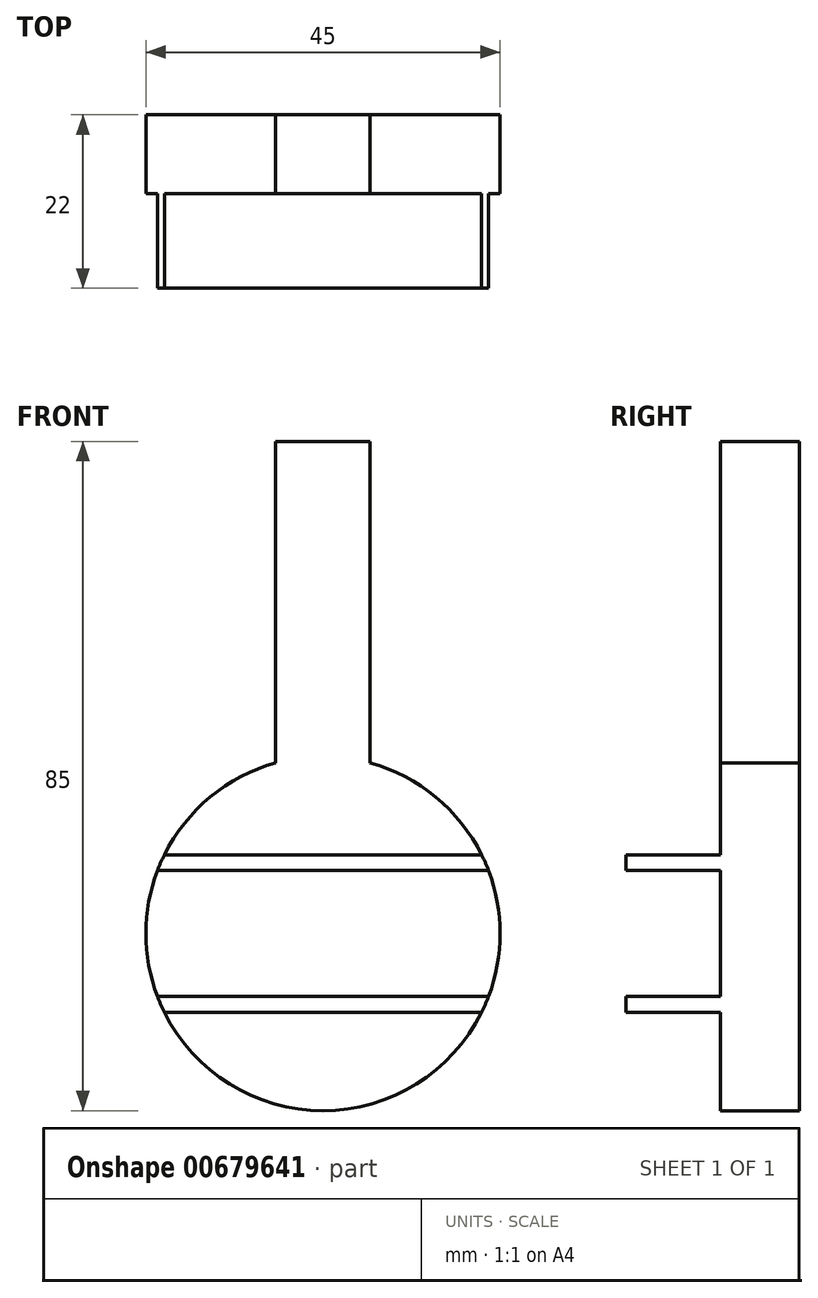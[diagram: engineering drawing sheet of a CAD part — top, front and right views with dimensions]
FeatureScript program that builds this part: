
annotation { "Feature Type Name" : "Feature", "Feature Type Description" : "" }
export const myFeature = defineFeature(function(context is Context, id is Id, definition is map)
    precondition{}
    {
        {
            var Q0;
            Q0=qCreatedBy(makeId("Front.planeOp"),FACE);
            var sketch = newSketch(context, id + "F0", { "sketchPlane" : qUnion([Q0])});
            skCircle(sketch, "E0", {"center": v(0, 0) * mm, "radius": 22.5 * mm});
            skLineSegment(sketch, "E1", {"start": v(-6, 22.5) * mm, "end": v(6, 22.5) * mm});
            skPoint(sketch, "E2", {"position": v(0, 22.5) * mm});
            skLineSegment(sketch, "E3", {"start": v(-6, 22.5) * mm, "end": v(-6, 21.69) * mm});
            skLineSegment(sketch, "E4", {"start": v(6, 22.5) * mm, "end": v(6, 21.69) * mm});
            skSolve(sketch);
        }
        {
            var Q0;
            Q0=makeQuery(id+"F0.imprint","IMPRINT",FACE,{"disambiguationData":[TD([[makeQuery(id+"F0.imprint","IMPRINT",EDGE,{"derivedFrom":sQuery(id+"F0.wireOp",EDGE,"E0")}),1.0]])]});
            extrude(context, id + "F1", {"entities" : qUnion([Q0]), "depth" : 10 * mm, "offsetDistance" : 25 * mm});
        }
        {
            var Q0;
            Q0=makeQuery(id+"F1.opExtrude","CAP_FACE",FACE,{"disambiguationData":[OSD([sQuery(id+"F0.wireOp",EDGE,"E0")])],"isStart":false});
            var sketch = newSketch(context, id + "F2", { "sketchPlane" : qUnion([Q0])});
            skLineSegment(sketch, "E5", {"start": v(-21.03, 8) * mm, "end": v(21.03, 8) * mm});
            skLineSegment(sketch, "E6", {"start": v(21.03, -8) * mm, "end": v(-21.03, -8) * mm});
            skLineSegment(sketch, "E7", {"start": v(-20.16, 10) * mm, "end": v(20.16, 10) * mm});
            skLineSegment(sketch, "E8", {"start": v(20.16, -10) * mm, "end": v(-20.16, -10) * mm});
            skLineSegment(sketch, "E9", {"start": v(-20.16, -8) * mm, "end": v(-20.16, -10) * mm});
            skLineSegment(sketch, "E10", {"start": v(20.16, -8) * mm, "end": v(20.16, -10) * mm});
            skLineSegment(sketch, "E11", {"start": v(-20.16, 10) * mm, "end": v(-20.16, 8) * mm});
            skLineSegment(sketch, "E12", {"start": v(20.16, 10) * mm, "end": v(20.16, 8) * mm});
            skSolve(sketch);
        }
        {
            var Q0;
            Q0=qSketchRegion(id+"F2",true);
            var Q1;
            {var subQ3=sQuery(id+"F2.wireOp",EDGE,"E12");Q1=makeQuery(id+"F2.imprint","IMPRINT",FACE,{"disambiguationData":[TD([[makeQuery(id+"F2.imprint","IMPRINT",EDGE,{"derivedFrom":subQ3}),1.0]])]});}
            var Q2;
            {var subQ3=sQuery(id+"F2.wireOp",EDGE,"E11");Q2=makeQuery(id+"F2.imprint","IMPRINT",FACE,{"disambiguationData":[TD([[makeQuery(id+"F2.imprint","IMPRINT",EDGE,{"derivedFrom":subQ3}),-1.0]])]});}
            var Q3;
            {var subQ3=sQuery(id+"F2.wireOp",EDGE,"E9");Q3=makeQuery(id+"F2.imprint","IMPRINT",FACE,{"disambiguationData":[TD([[makeQuery(id+"F2.imprint","IMPRINT",EDGE,{"derivedFrom":subQ3}),-1.0]])]});}
            var Q4;
            {var subQ3=sQuery(id+"F2.wireOp",EDGE,"E10");Q4=makeQuery(id+"F2.imprint","IMPRINT",FACE,{"disambiguationData":[TD([[makeQuery(id+"F2.imprint","IMPRINT",EDGE,{"derivedFrom":subQ3}),1.0]])]});}
            extrude(context, id + "F3", {"entities" : qUnion([Q0, Q1, Q2, Q3, Q4]), "operationType" : NewBodyOperationType.ADD, "depth" : 12 * mm, "offsetDistance" : 25 * mm});
        }
        {
            var Q0;
            Q0=makeQuery(id+"F1.opExtrude","CAP_FACE",FACE,{"disambiguationData":[OSD([sQuery(id+"F0.wireOp",EDGE,"E0")])],"isStart":true});
            var sketch = newSketch(context, id + "F4", { "sketchPlane" : qUnion([Q0])});
            skLineSegment(sketch, "E13", {"start": v(-21.94, 5) * mm, "end": v(21.94, 5) * mm});
            skLineSegment(sketch, "E14", {"start": v(-21.69, 6) * mm, "end": v(21.69, 6) * mm});
            skLineSegment(sketch, "E15", {"start": v(21.94, -5) * mm, "end": v(-21.94, -5) * mm});
            skLineSegment(sketch, "E16", {"start": v(-21.69, -6) * mm, "end": v(21.69, -6) * mm});
            skLineSegment(sketch, "E17", {"start": v(21.69, 6) * mm, "end": v(21.69, 5) * mm});
            skLineSegment(sketch, "E18", {"start": v(21.69, -5) * mm, "end": v(21.69, -6) * mm});
            skLineSegment(sketch, "E19", {"start": v(-21.69, 6) * mm, "end": v(-21.69, 5) * mm});
            skLineSegment(sketch, "E20", {"start": v(-21.69, -5) * mm, "end": v(-21.69, -6) * mm});
            skSolve(sketch);
        }
        {
            var Q0;
            Q0=qSketchRegion(id+"F4",true);
            var Q1;
            {var subQ3=sQuery(id+"F4.wireOp",EDGE,"E17");Q1=makeQuery(id+"F4.imprint","IMPRINT",FACE,{"disambiguationData":[TD([[makeQuery(id+"F4.imprint","IMPRINT",EDGE,{"derivedFrom":subQ3}),1.0]])]});}
            var Q2;
            {var subQ3=sQuery(id+"F4.wireOp",EDGE,"E18");Q2=makeQuery(id+"F4.imprint","IMPRINT",FACE,{"disambiguationData":[TD([[makeQuery(id+"F4.imprint","IMPRINT",EDGE,{"derivedFrom":subQ3}),1.0]])]});}
            var Q3;
            {var subQ3=sQuery(id+"F4.wireOp",EDGE,"E20");Q3=makeQuery(id+"F4.imprint","IMPRINT",FACE,{"disambiguationData":[TD([[makeQuery(id+"F4.imprint","IMPRINT",EDGE,{"derivedFrom":subQ3}),-1.0]])]});}
            var Q4;
            {var subQ3=sQuery(id+"F4.wireOp",EDGE,"E19");Q4=makeQuery(id+"F4.imprint","IMPRINT",FACE,{"disambiguationData":[TD([[makeQuery(id+"F4.imprint","IMPRINT",EDGE,{"derivedFrom":subQ3}),-1.0]])]});}
            extrude(context, id + "F5", {"entities" : qUnion([Q0, Q1, Q2, Q3, Q4]), "operationType" : NewBodyOperationType.ADD, "depth" : 4 * mm, "offsetDistance" : 25 * mm});
        }
        {
            var Q0;
            {var subQ0=sQuery(id+"F0.wireOp",EDGE,"E4");Q0=makeQuery(id+"F0.imprint","IMPRINT",FACE,{"disambiguationData":[TD([[makeQuery(id+"F0.imprint","IMPRINT",EDGE,{"derivedFrom":subQ0}),-1.0]])]});}
            var Q1;
            {var subQ0=sQuery(id+"F0.wireOp",EDGE,"E3");Q1=makeQuery(id+"F0.imprint","IMPRINT",FACE,{"disambiguationData":[TD([[makeQuery(id+"F0.imprint","IMPRINT",EDGE,{"derivedFrom":subQ0}),1.0]])]});}
            extrude(context, id + "F6", {"entities" : qUnion([Q0, Q1]), "operationType" : NewBodyOperationType.ADD, "depth" : 10 * mm, "offsetDistance" : 25 * mm});
        }
        {
            var Q0;
            {var subQ0=sQuery(id+"F0.wireOp",EDGE,"E1");Q0=makeQuery(id+"F6.boolean.opBoolean","MERGE",FACE,{"derivedFrom":[makeQuery(id+"F6.opExtrude","SWEPT_FACE",FACE,{"disambiguationData":[OSD([subQ0]),TDD([makeQuery(id+"F0.imprint","IMPRINT",EDGE,{"disambiguationData":[TD([[makeQuery(id+"F0.imprint","INTERSECT",VERTEX,{"derivedFrom":[subQ0,sQuery(id+"F0.wireOp",EDGE,"E3")]}),-1.0]])],"derivedFrom":subQ0})])]}),makeQuery(id+"F6.opExtrude","SWEPT_FACE",FACE,{"disambiguationData":[OSD([subQ0]),TDD([makeQuery(id+"F0.imprint","IMPRINT",EDGE,{"disambiguationData":[TD([[makeQuery(id+"F0.imprint","INTERSECT",VERTEX,{"derivedFrom":[subQ0,sQuery(id+"F0.wireOp",EDGE,"E4")]}),1.0]])],"derivedFrom":subQ0})])]})]});}
            var sketch = newSketch(context, id + "F7", { "sketchPlane" : qUnion([Q0])});
            skLineSegment(sketch, "E21.bottom", {"start": v(6, -10) * mm, "end": v(-6, -10) * mm});
            skLineSegment(sketch, "E21.top", {"start": v(6, 0) * mm, "end": v(-6, 0) * mm});
            skLineSegment(sketch, "E21.left", {"start": v(6, -10) * mm, "end": v(6, 0) * mm});
            skLineSegment(sketch, "E21.right", {"start": v(-6, -10) * mm, "end": v(-6, 0) * mm});
            skPoint(sketch, "E21.middle", {"position": v(0, -5) * mm});
            skPoint(sketch, "E21.middle.positionSnap0", {"position": v(-6, -5) * mm});
            skPoint(sketch, "E21.centerSnap0", {"position": v(-6, -5) * mm});
            skSolve(sketch);
        }
        {
            var Q0;
            Q0=qSketchRegion(id+"F7",true);
            extrude(context, id + "F8", {"entities" : qUnion([Q0]), "operationType" : NewBodyOperationType.ADD, "depth" : 40 * mm, "offsetDistance" : 25 * mm});
        }
        {
            var Q0;
            Q0=makeQuery(id+"F5.opExtrude","SWEPT_FACE",FACE,{"disambiguationData":[OSD([sQuery(id+"F4.wireOp",EDGE,"E14")])]});
            var sketch = newSketch(context, id + "F9", { "sketchPlane" : qUnion([Q0])});
            skLineSegment(sketch, "E22.bottom", {"start": v(28.97, 0) * mm, "end": v(-30.73, 0) * mm});
            skLineSegment(sketch, "E22.top", {"start": v(28.97, 7.6) * mm, "end": v(-30.73, 7.6) * mm});
            skLineSegment(sketch, "E22.left", {"start": v(28.97, 0) * mm, "end": v(28.97, 7.6) * mm});
            skLineSegment(sketch, "E22.right", {"start": v(-30.73, 0) * mm, "end": v(-30.73, 7.6) * mm});
            skSolve(sketch);
        }
        {
            var Q0;
            Q0 = qSketchRegion(id + "F9", true);
            extrude(context, id + "F10", {"entities" : qUnion([Q0]), "operationType" : NewBodyOperationType.REMOVE, "oppositeDirection" : true, "depth" : 25 * mm, "offsetDistance" : 25 * mm});
        }
    });
